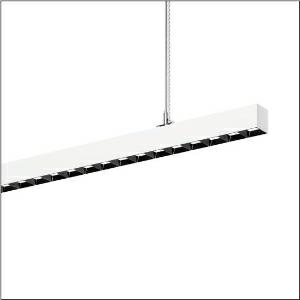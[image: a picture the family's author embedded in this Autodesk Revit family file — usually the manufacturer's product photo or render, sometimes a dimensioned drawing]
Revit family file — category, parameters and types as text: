
# Revit family: silica_r__21_51mx34dc4dwb_1888
name_source: partatom
category: Lighting Fixtures
units: mm (PartAtom-declared; Revit-internal decimal feet)

## family parameters
Cut with Voids When Loaded = No
Host = Face
Light Source = No
Part Type = Normal
Room Calculation Point = No
Round Connector Dimension = Use Diameter
Shared = No

## types (1)
- --- (1 x LED, 19200 lm, 120.3 W, 4000K)
    Apparent Load = 120 VA
    CIE Flux Codes = 74 94 99 56 100
    Color Rendering = 80
    Color Temperature = 4000K
    Default Elevation = 1800 mm
    Description = Silica® 21, office luminaire, primary light control with darklight reflector, of PMMA, black, light emission: direct/indirect distribution, primary light characteristic: asymmetric, installation type: suspended mounting, LED, rated luminous flux: 19.200lm, luminous efficacy: 160lm/W, light colour: 840, colour temperature: 4000K, control gear: DALI 2, with terminal, 3+2-pole, max. 2.5mm², mains connection: 220..240V, AC, 50/60Hz, rated input power: 120.3W, luminaire housing, of aluminium, traffic white (RAL 9016), length: 3.004mm, width: 53mm, height: 53mm, protection rating (complete): IP20, insulation class (complete): insulation class I (protective earthing), certification: CE, permissible operating ambient temperature: 0..+35°C, standard: EN 50419, packaging unit: 1 piece
    Height = 53 mm
    Lamp = 1 x LED
    Lamp Light Flux = 19200 lm
    Lamp Power = 120.3 W
    Lamp count = 1
    Length = 3004 mm
    Luminous efficacy = 160 lm/W
    Manufacturer = Siteco
    ModVariant = No
    Model = 51MX34DC4DWB
    Mounting Place = Ceiling
    Mounting Type = Pendant
    Number of Poles = 1
    OnlyDefault = Yes
    Power Factor = 1
    Product Name = Silica® 21
    Product group = office luminaire | ceiling pendant
    ProductGroupID = 904
    Protection Class = Protection class I
    Protection Degree = IP 20
    RLX_Detail_Level = 1
    RLX_Emergency_Light_Flux = 0 lm
    RLX_Emergency_Type = 0
    RLX_Emergency_Type_DB = No
    RlxData = <blob elided: 65513 chars, md5=1f7d3c0f>
    Socket = socket
    Standby Power = 0 W
    System Light Flux = 19200 lm
    System Power = 120 W
    Type Comments = factory setting: luminous flux: 100 % | dim-lin: 254 | 418 mA
    Type Image = l_1335871.jpg
    URL = http://relux.com
    VarID = @adj_120304
    Voltage = 0 V
    Weight = 0.00 kg
    Width = 53 mm

## geometry (parser evidence)
native form markers: Blend x4, Sweep x13
no freeform markers — native parametric forms only
